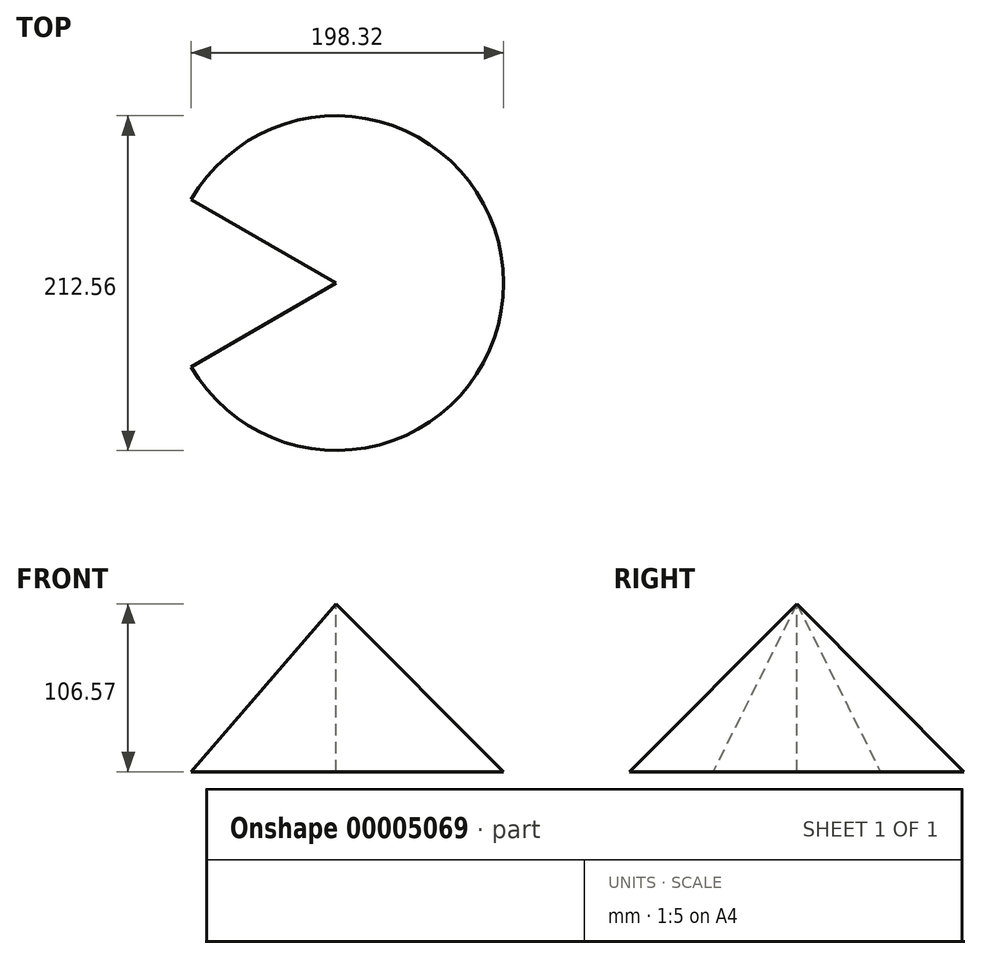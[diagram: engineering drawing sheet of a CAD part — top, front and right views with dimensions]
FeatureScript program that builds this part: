
annotation { "Feature Type Name" : "Feature", "Feature Type Description" : "" }
export const myFeature = defineFeature(function(context is Context, id is Id, definition is map)
    precondition{}
    {
        {
            var Q0;
            Q0=qCreatedBy(makeId("Front.planeOp"),FACE);
            var sketch = newSketch(context, id + "F0", { "sketchPlane" : qUnion([Q0])});
            skLineSegment(sketch, "E0", {"start": v(0, 0) * mm, "end": v(0, 106.57) * mm});
            skLineSegment(sketch, "E1", {"start": v(0, 106.57) * mm, "end": v(106.28, 0) * mm});
            skLineSegment(sketch, "E2", {"start": v(106.28, 0) * mm, "end": v(0, 0) * mm});
            skSolve(sketch);
        }
        {
            var Q0;
            Q0=makeQuery(id+"F0.imprint","IMPRINT",FACE,{"disambiguationData":[TD([[makeQuery(id+"F0.imprint","IMPRINT",EDGE,{"derivedFrom":sQuery(id+"F0.wireOp",EDGE,"E0")}),-1.0]])]});
            var Q1;
            Q1=sQuery(id+"F0.wireOp",EDGE,"E0");
            revolve(context, id + "F1", {"entities" : qUnion([Q0]), "axis" : qUnion([Q1]), "revolveType" : RevolveType.SYMMETRIC, "angle" : 300 * degree});
        }
    });
